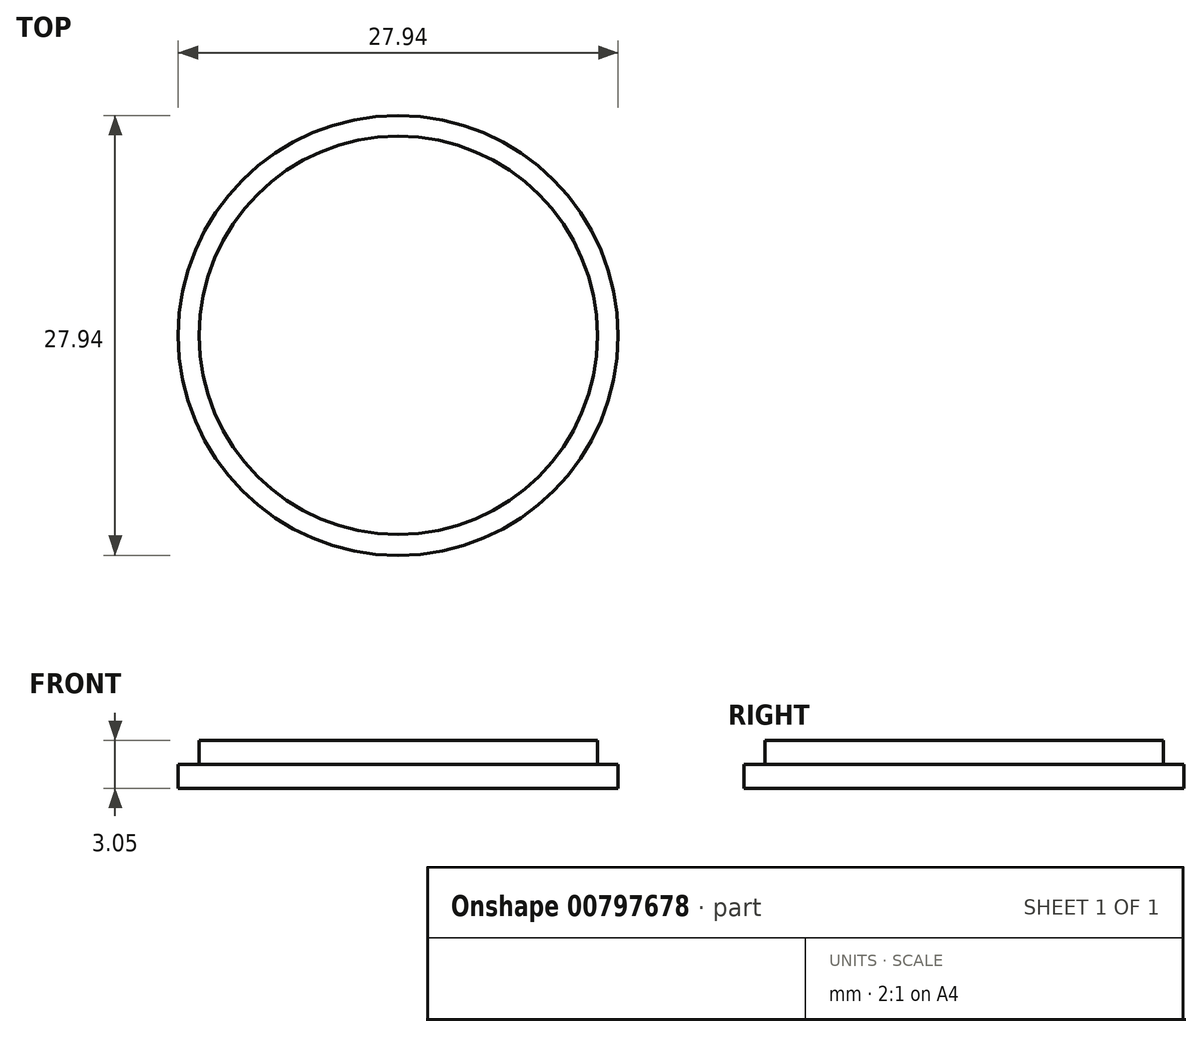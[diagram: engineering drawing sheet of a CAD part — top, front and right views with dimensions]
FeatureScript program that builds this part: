
annotation { "Feature Type Name" : "Feature", "Feature Type Description" : "" }
export const myFeature = defineFeature(function(context is Context, id is Id, definition is map)
    precondition{}
    {
        {
            var Q0;
            Q0=qCreatedBy(makeId("Top.planeOp"),FACE);
            var sketch = newSketch(context, id + "F0", { "sketchPlane" : qUnion([Q0])});
            skCircle(sketch, "E0", {"center": v(0, 0) * mm, "radius": 12.65 * mm});
            skSolve(sketch);
        }
        {
            var Q0;
            Q0=qSketchRegion(id+"F0",true);
            extrude(context, id + "F1", {"entities" : qUnion([Q0]), "depth" : 3.05 * mm, "offsetDistance" : 25.4 * mm});
        }
        {
            var Q0;
            Q0=qCreatedBy(makeId("Top.planeOp"),FACE);
            var sketch = newSketch(context, id + "F2", { "sketchPlane" : qUnion([Q0])});
            skCircle(sketch, "E1", {"center": v(0, 0) * mm, "radius": 13.97 * mm});
            skSolve(sketch);
        }
        {
            var Q0;
            Q0=qSketchRegion(id+"F2",true);
            extrude(context, id + "F3", {"entities" : qUnion([Q0]), "operationType" : NewBodyOperationType.ADD, "depth" : 1.52 * mm, "offsetDistance" : 25.4 * mm});
        }
    });
